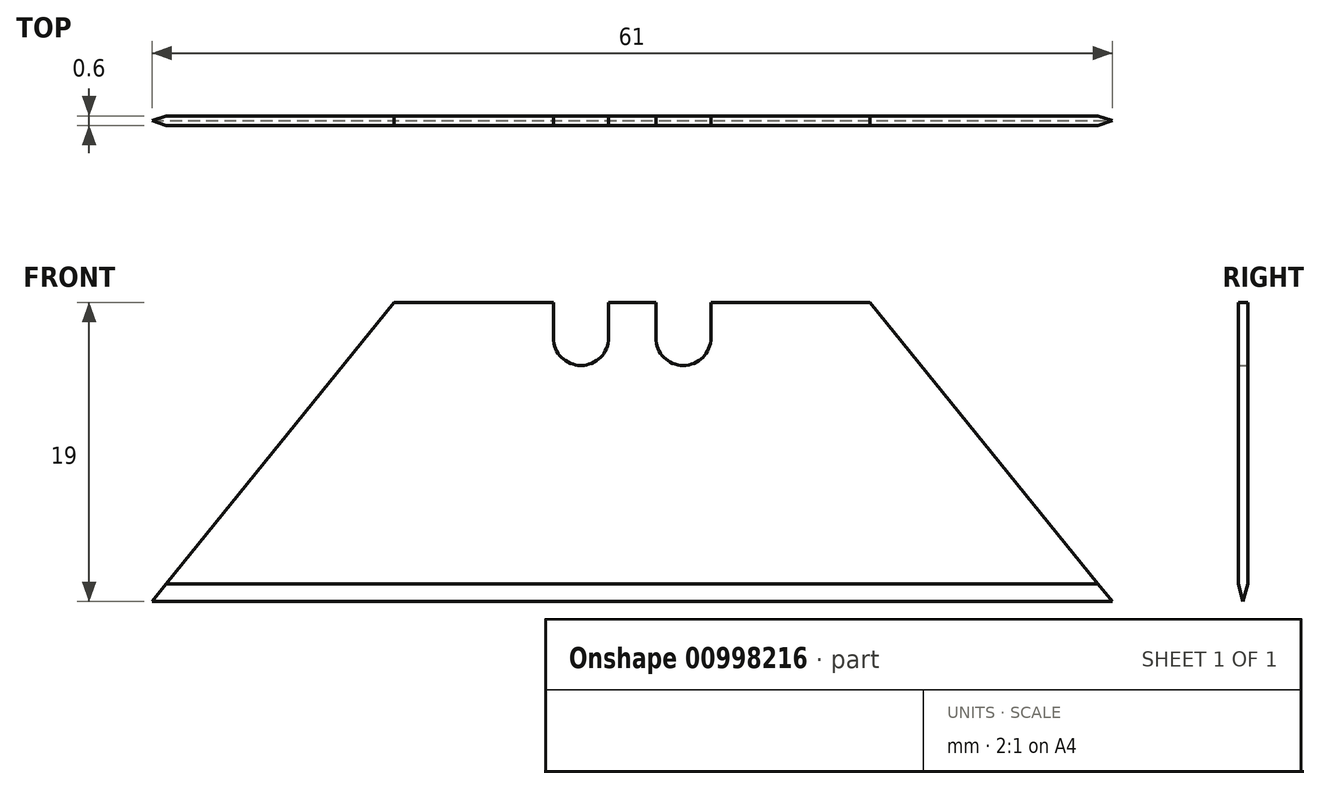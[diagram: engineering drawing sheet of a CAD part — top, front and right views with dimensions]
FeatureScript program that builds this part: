
annotation { "Feature Type Name" : "Feature", "Feature Type Description" : "" }
export const myFeature = defineFeature(function(context is Context, id is Id, definition is map)
    precondition{}
    {
        {
            var Q0;
            Q0=qCreatedBy(makeId("Front.planeOp"),FACE);
            var sketch = newSketch(context, id + "F0", { "sketchPlane" : qUnion([Q0])});
            skLineSegment(sketch, "E0.bottom", {"start": v(30.5, 9.5) * mm, "end": v(-30.5, 9.5) * mm});
            skLineSegment(sketch, "E0.top", {"start": v(30.5, -9.5) * mm, "end": v(-30.5, -9.5) * mm});
            skLineSegment(sketch, "E0.left", {"start": v(30.5, 9.5) * mm, "end": v(30.5, -9.5) * mm});
            skLineSegment(sketch, "E0.right", {"start": v(-30.5, 9.5) * mm, "end": v(-30.5, -9.5) * mm});
            skPoint(sketch, "E0.middle", {"position": v(0, 0) * mm});
            skLineSegment(sketch, "E1", {"start": v(0, 0) * mm, "end": v(0, 36.25) * mm, "construction": true});
            skLineSegment(sketch, "E2", {"start": v(30.5, -9.5) * mm, "end": v(15.11, 9.5) * mm});
            skLineSegment(sketch, "E3", {"start": v(3.25, 15.61) * mm, "end": v(3.25, 7.25) * mm});
            skArc(sketch, "E4.0.startCap", {"start": v(1.5, 15.61) * mm, "mid": v(3.25, 17.36) * mm, "end": v(5, 15.61) * mm});
            skArc(sketch, "E4.0.endCap", {"start": v(5, 7.25) * mm, "mid": v(3.25, 5.5) * mm, "end": v(1.5, 7.25) * mm});
            skLineSegment(sketch, "E4.0.left", {"start": v(5, 15.61) * mm, "end": v(5, 7.25) * mm});
            skLineSegment(sketch, "E4.0.right", {"start": v(1.5, 15.61) * mm, "end": v(1.5, 7.25) * mm});
            skLineSegment(sketch, "E5.MirrorCS", {"start": v(-1.5, 15.61) * mm, "end": v(-1.5, 7.25) * mm});
            skArc(sketch, "E6.MirrorCS", {"start": v(-5, 7.25) * mm, "mid": v(-3.25, 5.5) * mm, "end": v(-1.5, 7.25) * mm});
            skLineSegment(sketch, "E7.MirrorCS", {"start": v(-5, 15.61) * mm, "end": v(-5, 7.25) * mm});
            skArc(sketch, "E8.MirrorCS", {"start": v(-1.5, 15.61) * mm, "mid": v(-3.25, 17.36) * mm, "end": v(-5, 15.61) * mm});
            skLineSegment(sketch, "E9.MirrorCS", {"start": v(-30.5, -9.5) * mm, "end": v(-15.11, 9.5) * mm});
            skSolve(sketch);
        }
        {
            var Q0;
            Q0=makeQuery(id+"F0.imprint","IMPRINT",FACE,{"disambiguationData":[TD([[makeQuery(id+"F0.imprint","IMPRINT",EDGE,{"derivedFrom":sQuery(id+"F0.wireOp",EDGE,"E0.top")}),-1.0]])]});
            extrude(context, id + "F1", {"entities" : qUnion([Q0]), "depth" : 0.6 * mm, "offsetDistance" : 25 * mm});
        }
        {
            var Q0;
            Q0=qCreatedBy(makeId("Right.planeOp"),FACE);
            var sketch = newSketch(context, id + "F2", { "sketchPlane" : qUnion([Q0])});
            skLineSegment(sketch, "E10.0.0", {"start": v(0, -9.5) * mm, "end": v(0, 9.5) * mm});
            skLineSegment(sketch, "E10.0.1", {"start": v(0, 9.5) * mm, "end": v(-0.6, 9.5) * mm, "construction": true});
            skLineSegment(sketch, "E10.0.2", {"start": v(-0.6, 9.5) * mm, "end": v(-0.6, -9.5) * mm});
            skLineSegment(sketch, "E10.0.3", {"start": v(-0.6, -9.5) * mm, "end": v(0, -9.5) * mm});
            skLineSegment(sketch, "E11", {"start": v(-0.3, -9.5) * mm, "end": v(-0.3, -7.18) * mm, "construction": true});
            skLineSegment(sketch, "E12", {"start": v(-0.3, -9.5) * mm, "end": v(0, -8.38) * mm});
            skLineSegment(sketch, "E13", {"start": v(0, -8.38) * mm, "end": v(-0.3, -8.38) * mm});
            skLineSegment(sketch, "E14.MirrorCS", {"start": v(-0.6, -8.38) * mm, "end": v(-0.3, -8.38) * mm});
            skLineSegment(sketch, "E15.MirrorCS", {"start": v(-0.3, -9.5) * mm, "end": v(-0.6, -8.38) * mm});
            skSolve(sketch);
        }
        {
            var Q0;
            {var subQ3=sQuery(id+"F2.wireOp",EDGE,"E15.MirrorCS");Q0=makeQuery(id+"F2.imprint","IMPRINT",FACE,{"disambiguationData":[TD([[makeQuery(id+"F2.imprint","IMPRINT",EDGE,{"derivedFrom":subQ3}),1.0]])]});}
            var Q1;
            {var subQ3=sQuery(id+"F2.wireOp",EDGE,"E12");Q1=makeQuery(id+"F2.imprint","IMPRINT",FACE,{"disambiguationData":[TD([[makeQuery(id+"F2.imprint","IMPRINT",EDGE,{"derivedFrom":subQ3}),-1.0]])]});}
            extrude(context, id + "F3", {"entities" : qUnion([Q0, Q1]), "operationType" : NewBodyOperationType.REMOVE, "endBound" : BoundingType.THROUGH_ALL, "oppositeDirection" : true, "depth" : 25 * mm, "offsetDistance" : 25 * mm, "hasSecondDirection" : true, "secondDirectionBound" : SecondDirectionBoundingType.THROUGH_ALL, "secondDirectionOppositeDirection" : false, "secondDirectionDepth" : 25 * mm});
        }
    });
